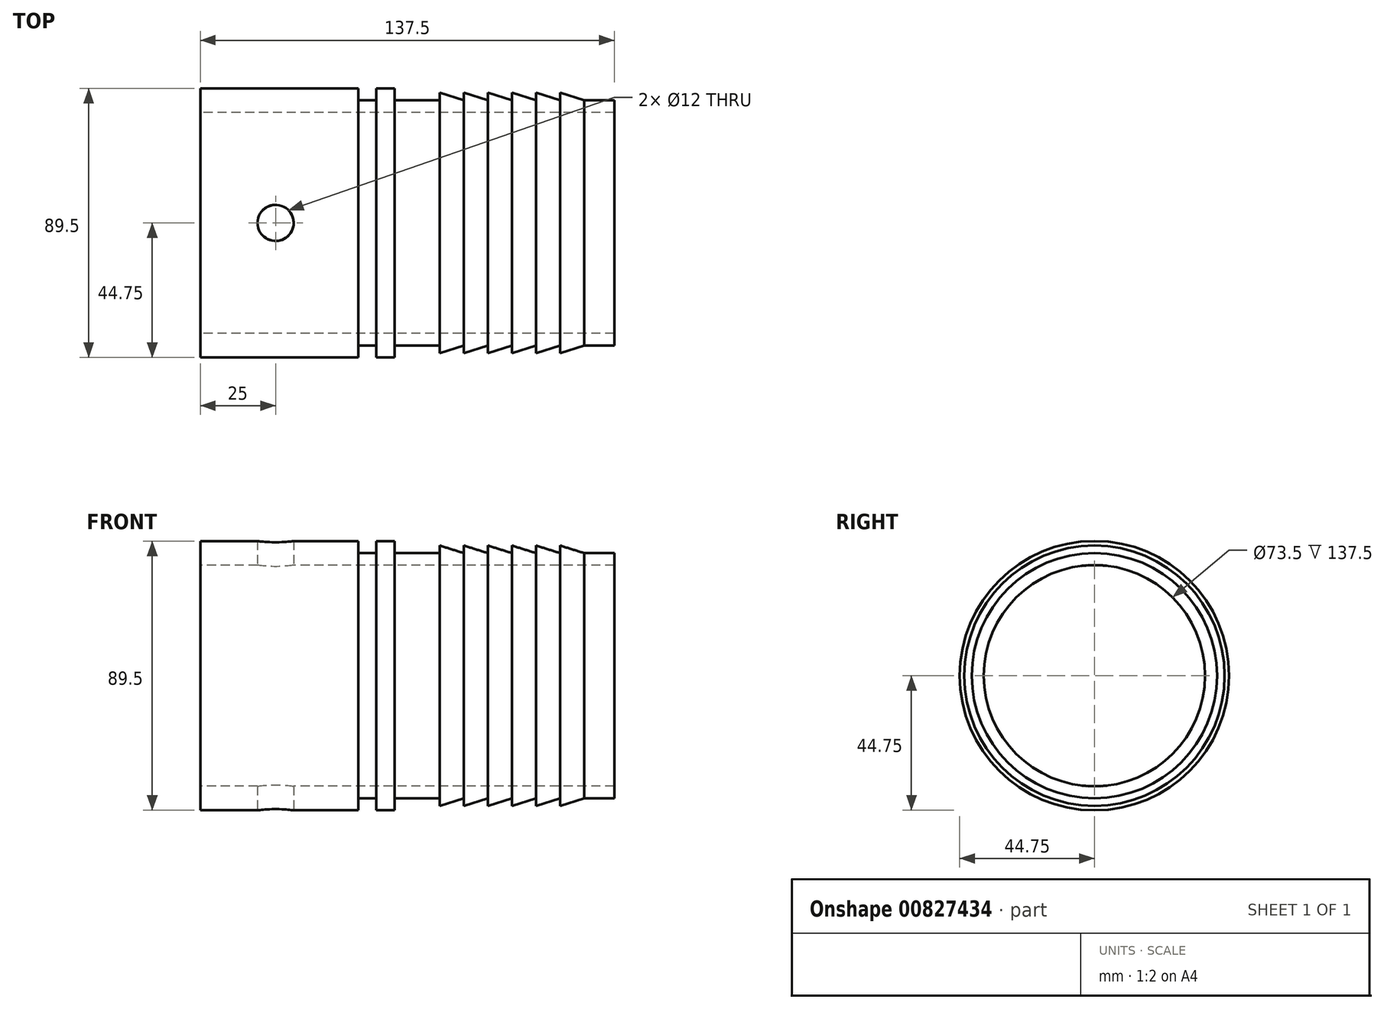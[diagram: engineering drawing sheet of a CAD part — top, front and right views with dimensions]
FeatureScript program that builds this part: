
annotation { "Feature Type Name" : "Feature", "Feature Type Description" : "" }
export const myFeature = defineFeature(function(context is Context, id is Id, definition is map)
    precondition{}
    {
        {
            var Q0;
            Q0=qCreatedBy(makeId("Front.planeOp"),FACE);
            var sketch = newSketch(context, id + "F0", { "sketchPlane" : qUnion([Q0])});
            skLineSegment(sketch, "E0", {"start": v(-86.07, 0) * mm, "end": v(128.54, 0) * mm, "construction": true});
            skLineSegment(sketch, "E1", {"start": v(0, 36.75) * mm, "end": v(0, 44.75) * mm});
            skLineSegment(sketch, "E2", {"start": v(52.5, 40.75) * mm, "end": v(58.5, 40.75) * mm});
            skLineSegment(sketch, "E3", {"start": v(58.5, 40.75) * mm, "end": v(58.5, 44.75) * mm});
            skLineSegment(sketch, "E4", {"start": v(58.5, 44.75) * mm, "end": v(64.5, 44.75) * mm});
            skLineSegment(sketch, "E5", {"start": v(64.5, 44.75) * mm, "end": v(64.5, 40.75) * mm});
            skLineSegment(sketch, "E6", {"start": v(64.5, 40.75) * mm, "end": v(79.5, 40.75) * mm});
            skLineSegment(sketch, "E7", {"start": v(79.5, 40.75) * mm, "end": v(79.5, 43.25) * mm});
            skLineSegment(sketch, "E8", {"start": v(79.5, 43.25) * mm, "end": v(87.5, 40.75) * mm});
            skLineSegment(sketch, "E9", {"start": v(87.5, 40.75) * mm, "end": v(87.5, 43.25) * mm});
            skLineSegment(sketch, "E10", {"start": v(87.5, 43.25) * mm, "end": v(95.5, 40.75) * mm});
            skLineSegment(sketch, "E11", {"start": v(95.5, 40.75) * mm, "end": v(95.5, 43.25) * mm});
            skLineSegment(sketch, "E12", {"start": v(95.5, 43.25) * mm, "end": v(103.5, 40.75) * mm});
            skLineSegment(sketch, "E13", {"start": v(103.5, 40.75) * mm, "end": v(103.5, 43.25) * mm});
            skLineSegment(sketch, "E14", {"start": v(103.5, 43.25) * mm, "end": v(111.5, 40.75) * mm});
            skLineSegment(sketch, "E15", {"start": v(111.5, 40.75) * mm, "end": v(111.5, 43.25) * mm});
            skLineSegment(sketch, "E16", {"start": v(111.5, 43.25) * mm, "end": v(119.5, 40.75) * mm});
            skLineSegment(sketch, "E17", {"start": v(119.5, 40.75) * mm, "end": v(119.5, 43.25) * mm});
            skLineSegment(sketch, "E18", {"start": v(119.5, 43.25) * mm, "end": v(127.5, 40.75) * mm});
            skLineSegment(sketch, "E19", {"start": v(127.5, 40.75) * mm, "end": v(137.5, 40.75) * mm});
            skLineSegment(sketch, "E20", {"start": v(137.5, 40.75) * mm, "end": v(137.5, 36.75) * mm});
            skLineSegment(sketch, "E21", {"start": v(137.5, 36.75) * mm, "end": v(0, 36.75) * mm});
            skLineSegment(sketch, "E22", {"start": v(52.5, 40.75) * mm, "end": v(52.5, 44.75) * mm});
            skLineSegment(sketch, "E23", {"start": v(52.5, 44.75) * mm, "end": v(0, 44.75) * mm});
            skSolve(sketch);
        }
        {
            var Q0;
            Q0=makeQuery(id+"F0.imprint","IMPRINT",FACE,{"disambiguationData":[TD([[makeQuery(id+"F0.imprint","IMPRINT",EDGE,{"derivedFrom":sQuery(id+"F0.wireOp",EDGE,"E1")}),-1.0]])]});
            var Q1;
            Q1=sQuery(id+"F0.wireOp",EDGE,"E0");
            revolve(context, id + "F1", {"surfaceOperationType" : NewSurfaceOperationType.NEW, "entities" : qUnion([Q0]), "axis" : qUnion([Q1]), "revolveType" : RevolveType.FULL});
        }
        {
            var Q0;
            Q0=qCreatedBy(makeId("Top.planeOp"),FACE);
            var sketch = newSketch(context, id + "F2", { "sketchPlane" : qUnion([Q0])});
            skCircle(sketch, "E24", {"center": v(25, 0) * mm, "radius": 6 * mm});
            skSolve(sketch);
        }
        {
            var Q0;
            Q0=makeQuery(id+"F2.imprint","IMPRINT",FACE,{"disambiguationData":[TD([[makeQuery(id+"F2.imprint","IMPRINT",EDGE,{"derivedFrom":sQuery(id+"F2.wireOp",EDGE,"E24")}),1.0]])]});
            extrude(context, id + "F3", {"entities" : qUnion([Q0]), "operationType" : NewBodyOperationType.REMOVE, "endBound" : BoundingType.SYMMETRIC, "depth" : 100 * mm, "offsetDistance" : 25 * mm});
        }
    });
